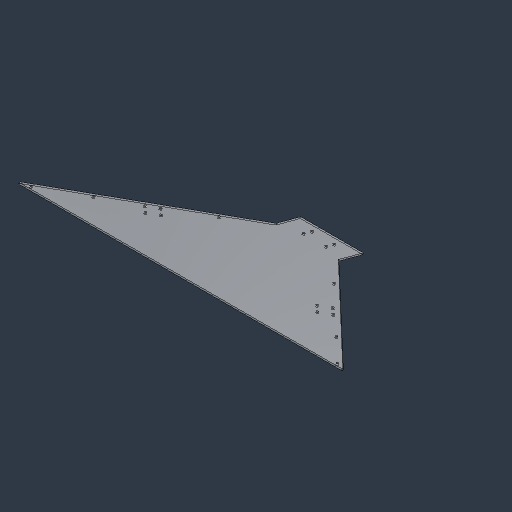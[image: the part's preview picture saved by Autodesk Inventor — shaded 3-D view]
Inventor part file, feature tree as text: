
AUTODESK INVENTOR PART (.ipt)
format: ipt  version: 2024.3 (Build 283343000, 343)  size: 271,360 bytes
history: native  units: in
note: dims shown in document units (in); Inventor stores cm internally (conversion verified against a paired STEP export)
features: sketch x5, other x5, hole x3, plane x2, mirror x2, sheet_metal_op x1, projected_geometry x1
ambient origin geometry x8: Origin, YZ Plane, XZ Plane, XY Plane, X Axis, Y Axis, Z Axis, Center Point
bodies: Solid1 (feature_tree)
feature tree (19):
  plane  "Work Plane1"
  sheet_metal_op  "Face1"
  hole  "Hole1"  [1 undecoded]
  hole  "Hole2"  [1 undecoded]
  plane  "Work Plane2"
  mirror  "Mirror1"
  hole  "Hole3"  [1 undecoded]
  mirror  "Mirror2"
  sketch  "Sketch1"  dims[d0=0.12in d1=2.5in]
  other  "Plate1"
  sketch  "Sketch2"  dims[d2=0.8125in d3=0.8125in]
  sketch  "Sketch3"  dims[d4=2.0in d5=0.7874in d7=0.75in d8=0.3937in d10=1.0in]
  projected_geometry  "Projected Loop1"
  sketch  "Sketch4"  dims[d12=1.0in]
  sketch  "Sketch5"  dims[d13=0.201in d14=0.75in d15=0.385in d16=0.25in d17=0.5635in d18=0.12in d19=0.8108in d20=0.5in d21=0.7874in d23=1.0in d24=0.7874in d26=1.0in d29=0.201in d30=0.75in d31=0.375in d32=0.25in d33=0.5635in d34=1.0in d35=0.8108in d36=0.25in d37=0.12in d38=0.0in d40=0.3505in d41=4.0in d42=0.75in d45=8.0in d46=0.201in d47=0.75in d48=0.375in d49=0.25in d50=0.5635in d51=0.12in d52=0.8108in]
  other  "Cut1"
  parser-record x1  (decoder bookkeeping rows leaked as tree rows — omitted from the tree; the rows remain in map.json)
  other  "#Poseidon 2025.iam"
  other  "hopper_side_r:1"
note: 3 required parameter values undecoded (feature->parameter linkage not recoverable at this tier; creation-order binding heuristic only, values carry confidence <= 0.55)
note: 1 file-system path scrubbed to <path> (originals preserved in map.json)
